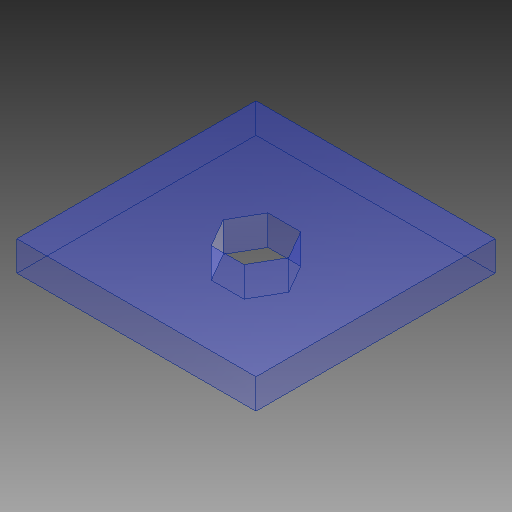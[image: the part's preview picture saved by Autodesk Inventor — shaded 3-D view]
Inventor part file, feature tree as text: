
AUTODESK INVENTOR PART (.ipt)
format: ipt  version: 2018.1 (Build 221171000, 171)  size: 108,544 bytes
history: native  units: mm
features: reference x6, other x4, extrude x2, sketch x2
ambient origin geometry x8: Origin, YZ Plane, XZ Plane, XY Plane, X Axis, Y Axis, Z Axis, Center Point
bodies: Solid1 (feature_tree)
feature tree (14):
  parser-record x2  (decoder bookkeeping rows leaked as tree rows — omitted from the tree; the rows remain in map.json)
  extrude  "Extrusion1"  TaperAngle=0.0deg  [1 undecoded]
  extrude  "Extrusion2"  TaperAngle=0.0deg  [1 undecoded]
  sketch  "Sketch1"  dims[d0=10.0mm d1=0.0mm]
  sketch  "Sketch2"  dims[d2=20.0mm d3=0.0mm d4=80.0mm d5=80.0mm]
  reference  "Reference1"
  reference  "Reference2"
  reference  "Reference3"
  reference  "Reference4"
  reference  "Reference5"
  reference  "Reference6"
  other  "Assembly - Load Cell.iam"
  other  "DIN 934 - replaced by DIN EN 24032/28673/28674 M12:1"
note: 2 required parameter values undecoded (feature->parameter linkage not recoverable at this tier; creation-order binding heuristic only, values carry confidence <= 0.55)
note: 2 file-system paths scrubbed to <path> (originals preserved in map.json)
